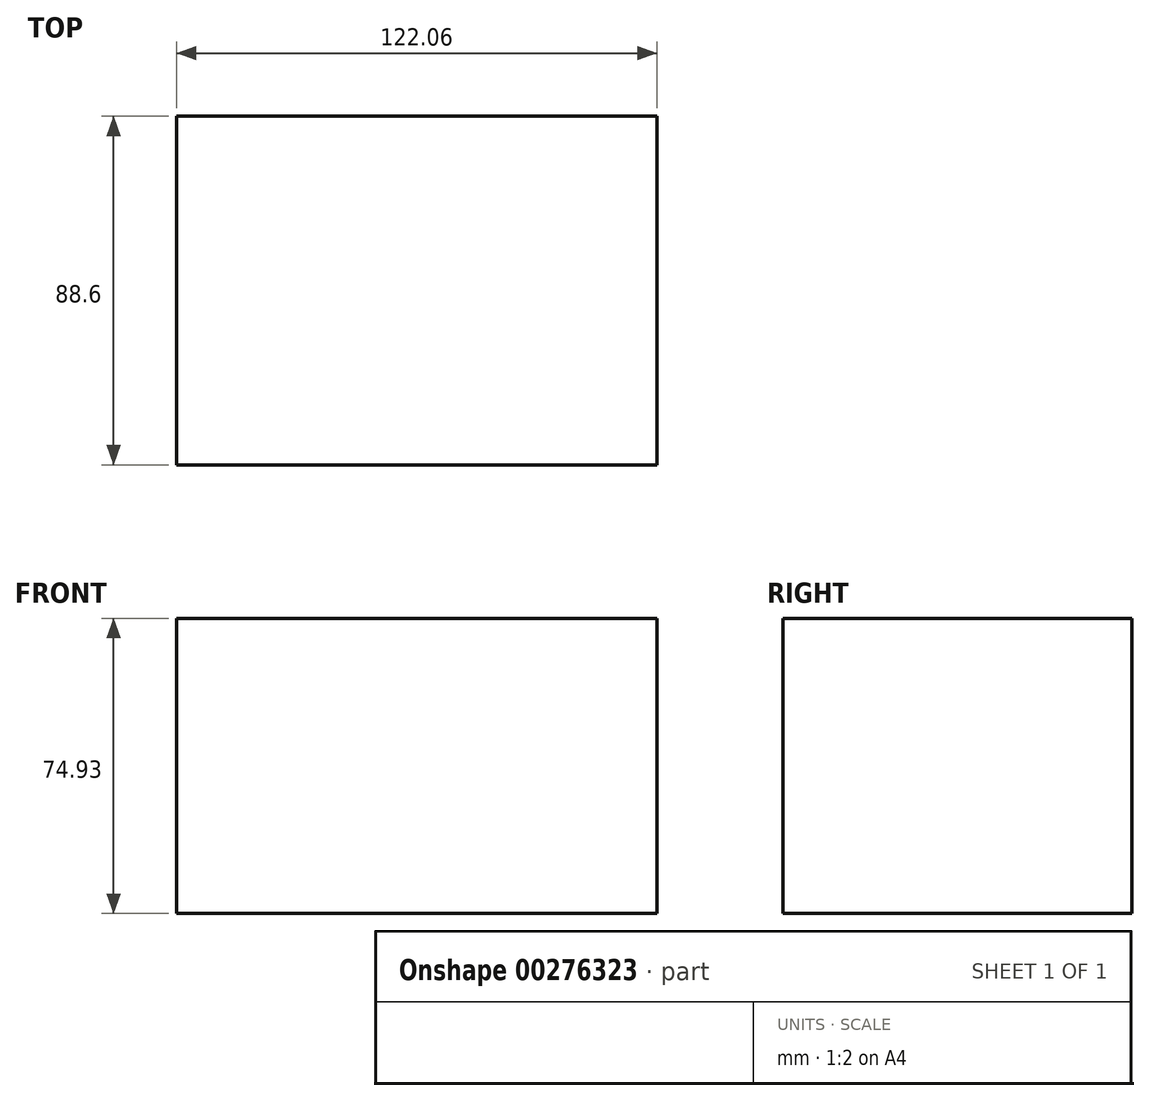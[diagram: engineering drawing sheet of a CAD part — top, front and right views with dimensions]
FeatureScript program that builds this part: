
annotation { "Feature Type Name" : "Feature", "Feature Type Description" : "" }
export const myFeature = defineFeature(function(context is Context, id is Id, definition is map)
    precondition{}
    {
        {
            var Q0;
            Q0=qCreatedBy(makeId("Top.planeOp"),FACE);
            var sketch = newSketch(context, id + "F0", { "sketchPlane" : qUnion([Q0])});
            skLineSegment(sketch, "E0.bottom", {"start": v(-43.23, 44.57) * mm, "end": v(53.43, 44.57) * mm});
            skLineSegment(sketch, "E0.top", {"start": v(-43.23, -44.03) * mm, "end": v(53.43, -44.03) * mm});
            skLineSegment(sketch, "E0.left", {"start": v(-43.23, 44.57) * mm, "end": v(-43.23, -44.03) * mm});
            skLineSegment(sketch, "E0.right", {"start": v(53.43, 44.57) * mm, "end": v(53.43, -44.03) * mm});
            skSolve(sketch);
        }
        {
            var Q0;
            Q0=makeQuery(id+"F0.imprint","IMPRINT",FACE,{"disambiguationData":[TD([[makeQuery(id+"F0.imprint","IMPRINT",EDGE,{"derivedFrom":sQuery(id+"F0.wireOp",EDGE,"E0.bottom")}),-1.0]])]});
            extrude(context, id + "F1", {"entities" : qUnion([Q0]), "depth" : 74.93 * mm});
        }
        {
            var Q0;
            Q0=makeQuery(id+"F1.opExtrude","SWEPT_FACE",FACE,{"disambiguationData":[OSD([sQuery(id+"F0.wireOp",EDGE,"E0.right")])]});
            extrude(context, id + "F2", {"entities" : qUnion([Q0]), "operationType" : NewBodyOperationType.ADD, "depth" : 25.4 * mm});
        }
        {
            var Q0;
            {var subQ0=sQuery(id+"F0.wireOp",EDGE,"E0.right");Q0=makeQuery(id+"F2.boolean.opBoolean","MERGE",FACE,{"derivedFrom":[makeQuery(id+"F1.opExtrude","CAP_FACE",FACE,{"disambiguationData":[OSD([sQuery(id+"F0.wireOp",EDGE,"E0.bottom"),sQuery(id+"F0.wireOp",EDGE,"E0.top"),sQuery(id+"F0.wireOp",EDGE,"E0.left"),subQ0])],"isStart":false}),makeQuery(id+"F2.opExtrude","SWEPT_FACE",FACE,{"disambiguationData":[OSD([subQ0]),TDD([makeQuery(id+"F1.opExtrude","CAP_EDGE",EDGE,{"disambiguationData":[OSD([subQ0])],"isStart":false})])]})]});}
            extrude(context, id + "F3", {"entities" : qUnion([Q0]), "operationType" : NewBodyOperationType.ADD, "oppositeDirection" : true, "depth" : 58.17 * mm});
        }
    });
